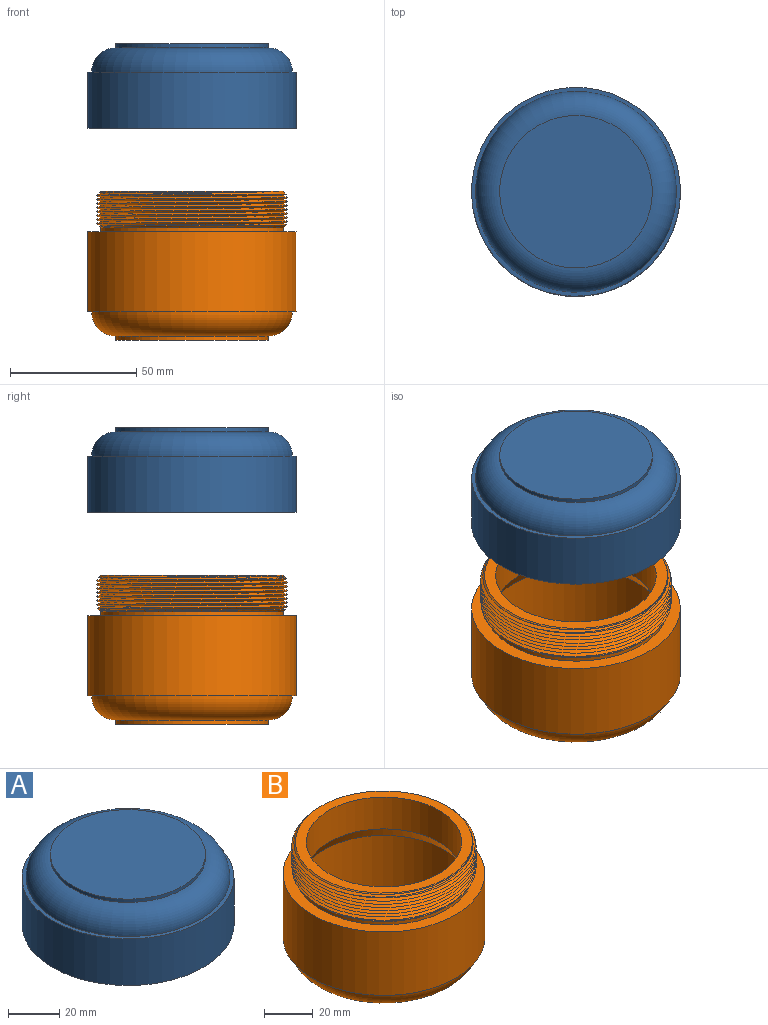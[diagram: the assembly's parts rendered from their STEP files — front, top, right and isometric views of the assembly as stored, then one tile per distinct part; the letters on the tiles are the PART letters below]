
ASSEMBLY  parts=2 mates=1
PART A: 12 faces, bbox 85.9x85.9x33.3 mm
  f0: cylinder r=41.27mm len=82.55mm, axis (0,0,-1), area 5763.8mm2, adj f1,f11
  f1: plane 82.55x82.55mm, normal (0,0,-1), area 1115.6mm2, adj f0,f2
  f2: cylinder r=36.72mm len=73.44mm, axis (0,0,-1), area 3298.8mm2, adj f1,f3
  f3: cone r=37.99mm half-angle=45deg, axis (0,0,1), area 421.6mm2, adj f2,f4
  f4: cylinder r=37.99mm len=75.98mm, axis (0,0,-1), area 73.5mm2, adj f3,f5
  f5: plane 75.98x75.98mm, normal (0,0,-1), area 1584mm2, adj f4,f6
  f6: cone r=30.65mm half-angle=45deg, axis (0,0,-1), area 2477.4mm2, adj f5,f7
  f7: plane 39.07x39.07mm, normal (0,0,-1), area 1198.7mm2, adj f6
  f8: plane 60.33x60.33mm, normal (0,0,1), area 2858.1mm2, adj f9
  f9: cylinder r=30.16mm len=60.33mm, axis (0,0,-1), area 300.9mm2, adj f8,f10
  f10: torus R=30.16mm, axis (0,0,-1), area 3405.6mm2, adj f9,f11
  f11: plane 82.55x82.55mm, normal (0,0,1), area 403.8mm2, adj f0,f10
PART B: 17 faces, bbox 85.9x87x59.5 mm
  f0: bspline ~87.01x75.36mm, area 2938.9mm2, adj f1,f2,f10
  f1: bspline ~87.01x75.36mm, area 2933.3mm2, adj f0,f2,f10
  f2: cone r=36.15mm half-angle=45deg, axis (0,0,-1), area 272.6mm2, adj f0,f1,f8
  f3: plane 63.5x63.5mm, normal (0,0,1), area 3166.9mm2, adj f4
  f4: torus R=31.75mm, axis (0,0,-1), area 1058.3mm2, adj f3,f5
  f5: cylinder r=34.92mm len=69.85mm, axis (0,0,-1), area 6108.8mm2, adj f4,f6
  f6: cone r=31.75mm half-angle=30deg, axis (0,0,-1), area 1330.1mm2, adj f5,f7
  f7: cylinder r=31.75mm len=63.5mm, axis (0,0,-1), area 3166.9mm2, adj f6,f8
  f8: plane 72.31x72.31mm, normal (0,0,1), area 939.4mm2, adj f2,f7
  f9: cylinder r=36.15mm len=72.3mm, axis (0,0,1), area 360.6mm2, adj f10,f16
  f10: cone r=36.15mm half-angle=45deg, axis (0,0,1), area 273.3mm2, adj f0,f1,f9
  f11: plane 60.33x60.33mm, normal (0,0,-1), area 2858.1mm2, adj f12
  f12: cylinder r=30.16mm len=60.33mm, axis (0,0,-1), area 300.9mm2, adj f11,f13
  f13: torus R=30.16mm, axis (0,0,-1), area 3405.6mm2, adj f12,f14
  f14: plane 82.55x82.55mm, normal (0,0,-1), area 403.8mm2, adj f13,f15
  f15: cylinder r=41.27mm len=82.55mm, axis (0,0,-1), area 8234mm2, adj f14,f16
  f16: plane 82.55x82.55mm, normal (0,0,1), area 1246.5mm2, adj f9,f15
PLACE A rot(axis=(0,0,1),101.5deg) t=(0,0,40.87)mm
PLACE B at identity fixed
MATE cylindrical A.f0 <-> B.f2  axis (0,0,-1) through (0,0,45.63)mm
